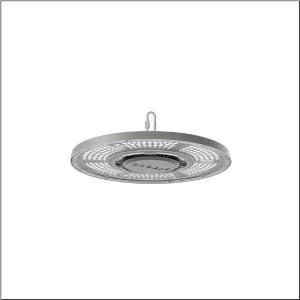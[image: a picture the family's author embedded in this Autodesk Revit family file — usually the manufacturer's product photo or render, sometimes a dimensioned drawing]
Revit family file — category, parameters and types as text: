
# Revit family: highbay_31-s_51hc41da4fmb
name_source: partatom
category: Lighting Fixtures
units: mm (PartAtom-declared; Revit-internal decimal feet)

## family parameters
Cut with Voids When Loaded = No
Host = Face
Light Source = No
Part Type = Normal
Room Calculation Point = No
Round Connector Dimension = Use Diameter
Shared = No

## types (1)
- Highbay 31-S (1 x LED, 14000 lm, 94 W, 4000K)
    Apparent Load = 94 VA
    CIE Flux Codes = 94 98 100 100 100
    Color Rendering = 80
    Color Temperature = 4000K
    Default Elevation = 1800 mm
    Description = Highbay 31-S, high bay luminaire, primary light control with lens, of PC, primary optical cover: cover panel, of PC, transparent, light emission: direct distribution, primary light characteristic: rotationally symmetric, installation type: suspended mounting, surface-mounted, LED, rated luminous flux: 14.000lm, luminous efficacy: 150lm/W, light colour: 840, colour temperature: 4000K, control gear: DALI 2, with cable, 5x 1.0mm², free wire ends, mains connection: 220..240V, AC, 50/60Hz, cable length: 1,5m, rated input power: 94W, housing, rotationally symmetric, of diecast aluminium, powder-coated, grey aluminium (RAL 9007), with hook on luminaire side, incl. screw, diameter: 339mm, protection rating (complete): IP65, insulation class (complete): insulation class I (protective earthing), certification: CE, ENEC, UKCA, protection symbol: D, impact resistance: IK08, permissible operating ambient temperature: -30..+45°C, corresponds to IFS (International Featured Standards) requirements for safety and quality in the food industry, packaging unit: 1 piece
    Height = 141 mm
    Lamp = 1 x LED
    Lamp Light Flux = 14000 lm
    Lamp Power = 94 W
    Lamp count = 1
    Length = 339 mm
    Luminous efficacy = 149 lm/W
    Manufacturer = Siteco
    ModVariant = No
    Model = 51HC41DA4FMB
    Mounting Place = Ceiling
    Mounting Type = Pendant
    Number of Poles = 1
    OnlyDefault = Yes
    Power Factor = 1
    Product Name = Highbay 31-S
    Product group = high bay luminaire
    ProductGroupID = 902
    Protection Class = Protection class I
    Protection Degree = IP 65
    RLX_Detail_Level = 1
    RLX_Emergency_Light_Flux = 0 lm
    RLX_Emergency_Type = 0
    RLX_Emergency_Type_DB = No
    RlxData = <blob elided: 107249 chars, md5=657b1236>
    Socket = socket
    Standby Power = 0 W
    System Light Flux = 14000 lm
    System Power = 94 W
    Type Comments = Product without accessories
    Type Image = l_1007237.jpg
    URL = http://relux.com
    VarID = ---
    Voltage = 0 V
    Weight = 0.00 kg
    Width = 0 mm  [stored 0 ft]

note: [stored X ft] marks values corroborated as IEEE doubles in the binary element streams (Revit-internal decimal feet)

## geometry (parser evidence)
native form markers: Blend x4, Sweep x10
no freeform markers — native parametric forms only
